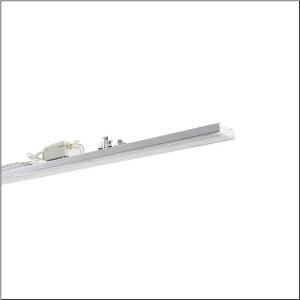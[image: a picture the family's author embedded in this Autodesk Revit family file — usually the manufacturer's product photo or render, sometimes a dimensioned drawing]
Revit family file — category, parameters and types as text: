
# Revit family: licross_11_recessed_mo_51te12dn4axg
name_source: partatom
category: Lighting Fixtures
units: mm (PartAtom-declared; Revit-internal decimal feet)

## family parameters
Cut with Voids When Loaded = No
Host = Face
Light Source = No
Part Type = Normal
Room Calculation Point = No
Round Connector Dimension = Use Diameter
Shared = No

## types (1)
- --- (1 x LED, 10240 lm, 56.7 W, 4000K)
    Apparent Load = 57 VA
    CIE Flux Codes = 67 92 99 100 100
    Color Rendering = 80
    Color Temperature = 4000K
    Default Elevation = 1800 mm
    Description = Licross 11 Recessed MO, luminaire insert, of sheet steel, galvanised, coil coated, white, length: 1.500mm, width: 66mm, height: 67mm, LED rated luminous flux: 10.240lm, light colour: 840, SDCM (Standard Deviation of Colour Matching)MacAdam ≤ 2 SDCM (initial), control gear: DALI 2, with plug, 5-pole, with phase selection, mains connection: 220..240V, AC, 50/60Hz, rated input power: 57W, internal wiring halogen-free, primary optical cover: cover, of PMMA, light emission: direct distribution, primary light characteristic: symmetric, protection rating (complete): IP54, insulation class (complete): insulation class I (protective earthing), certification: CE, ENEC, VDE, UKCA, protection symbol: D if used in an environment with non-conductive dust loads with corresponding accessories, impact resistance: IK06, permissible ambient temperature for indoor applications: -25..+35°C, corresponds to IFS (International Featured Standards) requirements for safety and quality in the food industry, reducing of maximum allowable ambient temperature of 5°C with ceiling mounting, LABS conformity tested according to VDMA 24364:2018-05, The light source and the operating device comply with the requirements of the Ecodesign Regulation (EU) 2019/2020 and are replaceable in accordance with this regulation, packaging unit: 1 piece
    Height = 58 mm
    Lamp = 1 x LED
    Lamp Light Flux = 10240 lm
    Lamp Power = 56.7 W
    Lamp count = 1
    Length = 1500 mm
    Luminous efficacy = 181 lm/W
    Manufacturer = Siteco
    ModVariant = No
    Model = 51TE12DN4AXG
    Mounting Place = Ceiling
    Mounting Type = Pendant
    Number of Poles = 1
    OnlyDefault = Yes
    Power Factor = 1
    Product Name = Licross 11 Recessed MO
    Product group = luminaire insert | ceiling pendant
    ProductGroupID = 901
    Protection Class = Protection class I
    Protection Degree = IP 54
    RLX_Detail_Level = 1
    RLX_Emergency_Light_Flux = 0 lm
    RLX_Emergency_Type = 0
    RLX_Emergency_Type_DB = No
    RlxData = <blob elided: 24657 chars, md5=41a551de>
    Socket = socket
    Standby Power = 0 W
    System Light Flux = 10240 lm
    System Power = 57 W
    Type Comments = factory setting: luminous flux: 100 % | dim-lin: 254 | 378 mA
    Type Image = l_1296930.jpg
    URL = http://relux.com
    VarID = @adj_103367
    Voltage = 0 V
    Weight = 0.00 kg
    Width = 66 mm

## geometry (parser evidence)
native form markers: Blend x4, Sweep x11
no freeform markers — native parametric forms only
